# Revit family: nbl_TritonSystems_AquaPumpProPlusKit
name_source: partatom
category: Plumbing Fixtures
revit_build: Autodesk Revit Architecture 2012 (Build: 20110309_2315(x64)
units: mm (PartAtom-declared; Revit-internal decimal feet)

## types (1)
- nbl_TritonSystems_AquaPumpProPlusKit
    BIMObjectName = nbl_TritonSystems_AquaPumpProPlusKit
    CasingMaterial = Fibre reinforced plastic
    Colour = Red
    ConnectionSize = 32
    Description = Pump system for removal of water from buildings
    DischargePipe = 32 mm
    DocumentReference = www.tritonsystems.co.uk
    Documentation = www.tritonsystems.co.uk/pdf/Triton_Pumps_Brochure.pdf
    ElectricalDeviceNominalPower = 0
    FlowRateRange = 0
    FlowResistanceRange = 0
    HasProtectiveEarth = Yes
    Help = www.nationalBIMlibrary.com
    ImpellerMaterial = Fibre reinforced plastic
    ImpellerSealMaterial = Silicon carbide on silicon carbide. Ceramic on carbon
    IssueDate = 2012-11-26
    Manufacturer = Triton Systems
    ManufacturerURL = www.tritonsystems.co.uk
    ModelReference = Triton Aqua Pump Pro Plus Kit
    NBSDescription = Submersible pumps
    NBSReference = 90-10-70/430
    NetPositiveSuctionHead = 0
    NominalCurrent = 0
    NominalFrequencyRange = 0
    NominalHeight = 0 mm  [stored 0 ft]
    NominalRotationSpeed = 2850
    NominalVoltage = 0
    NominalWidth = 0 mm  [stored 0 ft]
    NumberOfPoles = 0
    PhaseAngle = 0.00°
    PumpCapacity = 132 L/m
    TemperatureRange = 0
    UsageCurrent = 0
    Version = 1.0

note: [stored X ft] marks values corroborated as IEEE doubles in the binary element streams (Revit-internal decimal feet)

## geometry (parser evidence)
native form markers: Sweep x3
no freeform markers — native parametric forms only
